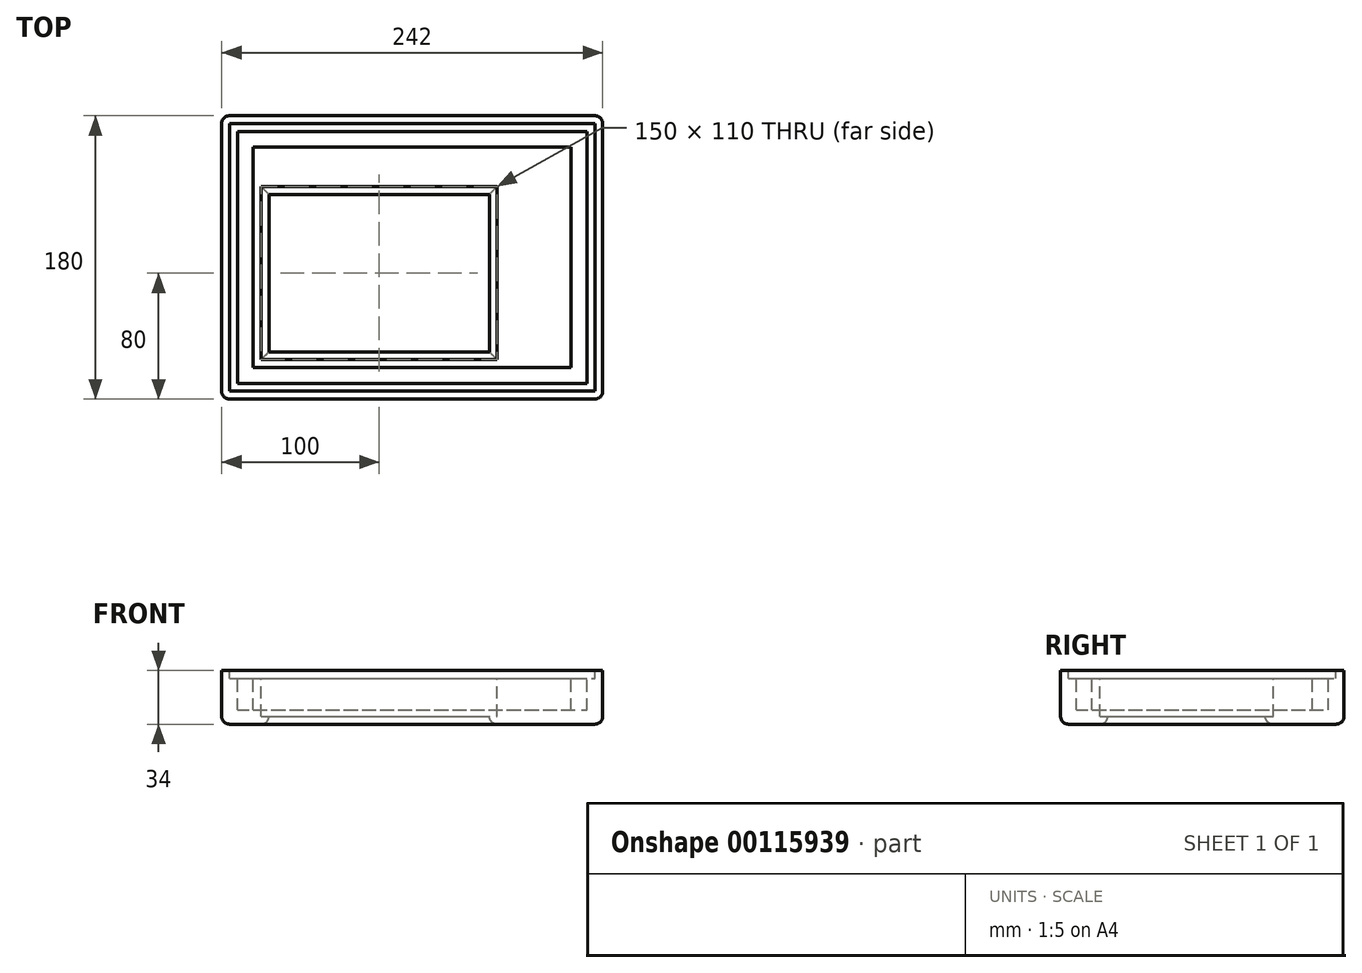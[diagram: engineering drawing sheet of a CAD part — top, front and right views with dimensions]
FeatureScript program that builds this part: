
annotation { "Feature Type Name" : "Feature", "Feature Type Description" : "" }
export const myFeature = defineFeature(function(context is Context, id is Id, definition is map)
    precondition{}
    {
        {
            var Q0;
            Q0=qCreatedBy(makeId("Top.planeOp"),FACE);
            var sketch = newSketch(context, id + "F0", { "sketchPlane" : qUnion([Q0])});
            skLineSegment(sketch, "E0.bottom", {"start": v(0, 0) * mm, "end": v(242, 0) * mm});
            skLineSegment(sketch, "E0.top", {"start": v(0, 180) * mm, "end": v(242, 180) * mm});
            skLineSegment(sketch, "E0.left", {"start": v(0, 0) * mm, "end": v(0, 180) * mm});
            skLineSegment(sketch, "E0.right", {"start": v(242, 0) * mm, "end": v(242, 180) * mm});
            skSolve(sketch);
        }
        {
            var Q0;
            Q0=makeQuery(id+"F0.imprint","IMPRINT",FACE,{"disambiguationData":[TD([[makeQuery(id+"F0.imprint","IMPRINT",EDGE,{"derivedFrom":sQuery(id+"F0.wireOp",EDGE,"E0.bottom")}),1.0]])]});
            extrude(context, id + "F1", {"entities" : qUnion([Q0]), "depth" : 34 * mm});
        }
        {
            var Q0;
            Q0=makeQuery(id+"F1.opExtrude","CAP_FACE",FACE,{"disambiguationData":[OSD([sQuery(id+"F0.wireOp",EDGE,"E0.bottom"),sQuery(id+"F0.wireOp",EDGE,"E0.top"),sQuery(id+"F0.wireOp",EDGE,"E0.left"),sQuery(id+"F0.wireOp",EDGE,"E0.right")])],"isStart":false});
            var sketch = newSketch(context, id + "F2", { "sketchPlane" : qUnion([Q0])});
            skPoint(sketch, "E1", {"position": v(30, 30) * mm});
            skLineSegment(sketch, "E2.bottom", {"start": v(30, 30) * mm, "end": v(170, 30) * mm});
            skLineSegment(sketch, "E2.top", {"start": v(30, 130) * mm, "end": v(170, 130) * mm});
            skLineSegment(sketch, "E2.left", {"start": v(30, 30) * mm, "end": v(30, 130) * mm});
            skLineSegment(sketch, "E2.right", {"start": v(170, 30) * mm, "end": v(170, 130) * mm});
            skSolve(sketch);
        }
        {
            var Q0;
            Q0=makeQuery(id+"F2.imprint","IMPRINT",FACE,{"disambiguationData":[TD([[makeQuery(id+"F2.imprint","IMPRINT",EDGE,{"derivedFrom":sQuery(id+"F2.wireOp",EDGE,"E2.bottom")}),1.0]])]});
            extrude(context, id + "F3", {"entities" : qUnion([Q0]), "operationType" : NewBodyOperationType.REMOVE, "endBound" : BoundingType.THROUGH_ALL, "oppositeDirection" : true, "depth" : 29 * mm});
        }
        {
            var Q0;
            Q0=makeQuery(id+"F1.opExtrude","CAP_FACE",FACE,{"disambiguationData":[OSD([sQuery(id+"F0.wireOp",EDGE,"E0.bottom"),sQuery(id+"F0.wireOp",EDGE,"E0.top"),sQuery(id+"F0.wireOp",EDGE,"E0.left"),sQuery(id+"F0.wireOp",EDGE,"E0.right")])],"isStart":false});
            var sketch = newSketch(context, id + "F4", { "sketchPlane" : qUnion([Q0])});
            skPoint(sketch, "E3", {"position": v(25, 25) * mm});
            skLineSegment(sketch, "E4.bottom", {"start": v(25, 25) * mm, "end": v(175, 25) * mm});
            skLineSegment(sketch, "E4.top", {"start": v(25, 135) * mm, "end": v(175, 135) * mm});
            skLineSegment(sketch, "E4.left", {"start": v(25, 25) * mm, "end": v(25, 135) * mm});
            skLineSegment(sketch, "E4.right", {"start": v(175, 25) * mm, "end": v(175, 135) * mm});
            skSolve(sketch);
        }
        {
            var Q0;
            Q0=makeQuery(id+"F4.imprint","IMPRINT",FACE,{"disambiguationData":[TD([[makeQuery(id+"F4.imprint","IMPRINT",EDGE,{"derivedFrom":sQuery(id+"F4.wireOp",EDGE,"E4.bottom")}),1.0]])]});
            extrude(context, id + "F5", {"entities" : qUnion([Q0]), "operationType" : NewBodyOperationType.REMOVE, "oppositeDirection" : true, "depth" : 29 * mm});
        }
        {
            var Q0;
            Q0=makeQuery(id+"F1.opExtrude","CAP_FACE",FACE,{"disambiguationData":[OSD([sQuery(id+"F0.wireOp",EDGE,"E0.bottom"),sQuery(id+"F0.wireOp",EDGE,"E0.top"),sQuery(id+"F0.wireOp",EDGE,"E0.left"),sQuery(id+"F0.wireOp",EDGE,"E0.right")])],"isStart":false});
            var sketch = newSketch(context, id + "F6", { "sketchPlane" : qUnion([Q0])});
            skPoint(sketch, "E5", {"position": v(5, 5) * mm});
            skLineSegment(sketch, "E6.bottom", {"start": v(5, 5) * mm, "end": v(237, 5) * mm});
            skLineSegment(sketch, "E6.top", {"start": v(5, 175) * mm, "end": v(237, 175) * mm});
            skLineSegment(sketch, "E6.left", {"start": v(5, 5) * mm, "end": v(5, 175) * mm});
            skLineSegment(sketch, "E6.right", {"start": v(237, 5) * mm, "end": v(237, 175) * mm});
            skSolve(sketch);
        }
        {
            var Q0;
            Q0=makeQuery(id+"F6.imprint","IMPRINT",FACE,{"disambiguationData":[TD([[makeQuery(id+"F6.imprint","IMPRINT",EDGE,{"derivedFrom":sQuery(id+"F6.wireOp",EDGE,"E6.bottom")}),1.0]])]});
            extrude(context, id + "F7", {"entities" : qUnion([Q0]), "operationType" : NewBodyOperationType.REMOVE, "oppositeDirection" : true, "depth" : 5 * mm});
        }
        {
            var Q0;
            Q0=makeQuery(id+"F7.boolean.opBoolean","COPY",FACE,{"derivedFrom":makeQuery(id+"F7.opExtrude","CAP_FACE",FACE,{"disambiguationData":[OSD([sQuery(id+"F4.wireOp",EDGE,"E4.bottom"),sQuery(id+"F4.wireOp",EDGE,"E4.top"),sQuery(id+"F4.wireOp",EDGE,"E4.left"),sQuery(id+"F4.wireOp",EDGE,"E4.right"),sQuery(id+"F6.wireOp",EDGE,"E6.bottom"),sQuery(id+"F6.wireOp",EDGE,"E6.top"),sQuery(id+"F6.wireOp",EDGE,"E6.left"),sQuery(id+"F6.wireOp",EDGE,"E6.right")])],"isStart":false})});
            var sketch = newSketch(context, id + "F8", { "sketchPlane" : qUnion([Q0])});
            skPoint(sketch, "E7", {"position": v(10, 10) * mm});
            skPoint(sketch, "E8", {"position": v(20, 20) * mm});
            skLineSegment(sketch, "E9.bottom", {"start": v(20, 20) * mm, "end": v(222, 20) * mm});
            skLineSegment(sketch, "E9.top", {"start": v(20, 160) * mm, "end": v(222, 160) * mm});
            skLineSegment(sketch, "E9.left", {"start": v(20, 20) * mm, "end": v(20, 160) * mm});
            skLineSegment(sketch, "E9.right", {"start": v(222, 20) * mm, "end": v(222, 160) * mm});
            skLineSegment(sketch, "E10.bottom", {"start": v(10, 10) * mm, "end": v(232, 10) * mm});
            skLineSegment(sketch, "E10.top", {"start": v(10, 170) * mm, "end": v(232, 170) * mm});
            skLineSegment(sketch, "E10.left", {"start": v(10, 10) * mm, "end": v(10, 170) * mm});
            skLineSegment(sketch, "E10.right", {"start": v(232, 10) * mm, "end": v(232, 170) * mm});
            skSolve(sketch);
        }
        {
            var Q0;
            Q0=makeQuery(id+"F8.imprint","IMPRINT",FACE,{"disambiguationData":[TD([[makeQuery(id+"F8.imprint","IMPRINT",EDGE,{"derivedFrom":sQuery(id+"F8.wireOp",EDGE,"E9.bottom")}),-1.0]])]});
            extrude(context, id + "F9", {"entities" : qUnion([Q0]), "operationType" : NewBodyOperationType.REMOVE, "oppositeDirection" : true, "depth" : 20 * mm});
        }
        {
            var Q0;
            Q0=makeQuery(id+"F1.opExtrude","SWEPT_EDGE",EDGE,{"disambiguationData":[OSD([sQuery(id+"F0.wireOp",EDGE,"E0.bottom"),sQuery(id+"F0.wireOp",EDGE,"E0.right")])]});
            var Q1;
            Q1=makeQuery(id+"F1.opExtrude","SWEPT_EDGE",EDGE,{"disambiguationData":[OSD([sQuery(id+"F0.wireOp",EDGE,"E0.top"),sQuery(id+"F0.wireOp",EDGE,"E0.right")])]});
            var Q2;
            Q2=makeQuery(id+"F1.opExtrude","SWEPT_EDGE",EDGE,{"disambiguationData":[OSD([sQuery(id+"F0.wireOp",EDGE,"E0.top"),sQuery(id+"F0.wireOp",EDGE,"E0.left")])]});
            var Q3;
            Q3=makeQuery(id+"F1.opExtrude","SWEPT_EDGE",EDGE,{"disambiguationData":[OSD([sQuery(id+"F0.wireOp",EDGE,"E0.bottom"),sQuery(id+"F0.wireOp",EDGE,"E0.left")])]});
            fillet(context, id + "F10", {"entities" : qUnion([Q0, Q1, Q2, Q3]), "radius" : 5 * mm, "tangentPropagation" : true, "allowEdgeOverflow" : false});
        }
        {
            var Q0;
            Q0=makeQuery(id+"F1.opExtrude","CAP_EDGE",EDGE,{"disambiguationData":[OSD([sQuery(id+"F0.wireOp",EDGE,"E0.bottom")])],"isStart":true});
            var Q1;
            Q1=makeQuery(id+"F3.boolean.opBoolean","INTERSECT",EDGE,{"derivedFrom":[makeQuery(id+"F1.opExtrude","CAP_FACE",FACE,{"disambiguationData":[OSD([sQuery(id+"F0.wireOp",EDGE,"E0.bottom"),sQuery(id+"F0.wireOp",EDGE,"E0.top"),sQuery(id+"F0.wireOp",EDGE,"E0.left"),sQuery(id+"F0.wireOp",EDGE,"E0.right")])],"isStart":true}),makeQuery(id+"F3.opExtrude","SWEPT_FACE",FACE,{"disambiguationData":[OSD([sQuery(id+"F2.wireOp",EDGE,"E2.right")])]})]});
            var Q2;
            Q2=makeQuery(id+"F3.boolean.opBoolean","INTERSECT",EDGE,{"derivedFrom":[makeQuery(id+"F1.opExtrude","CAP_FACE",FACE,{"disambiguationData":[OSD([sQuery(id+"F0.wireOp",EDGE,"E0.bottom"),sQuery(id+"F0.wireOp",EDGE,"E0.top"),sQuery(id+"F0.wireOp",EDGE,"E0.left"),sQuery(id+"F0.wireOp",EDGE,"E0.right")])],"isStart":true}),makeQuery(id+"F3.opExtrude","SWEPT_FACE",FACE,{"disambiguationData":[OSD([sQuery(id+"F2.wireOp",EDGE,"E2.bottom")])]})]});
            var Q3;
            Q3=makeQuery(id+"F3.boolean.opBoolean","INTERSECT",EDGE,{"derivedFrom":[makeQuery(id+"F1.opExtrude","CAP_FACE",FACE,{"disambiguationData":[OSD([sQuery(id+"F0.wireOp",EDGE,"E0.bottom"),sQuery(id+"F0.wireOp",EDGE,"E0.top"),sQuery(id+"F0.wireOp",EDGE,"E0.left"),sQuery(id+"F0.wireOp",EDGE,"E0.right")])],"isStart":true}),makeQuery(id+"F3.opExtrude","SWEPT_FACE",FACE,{"disambiguationData":[OSD([sQuery(id+"F2.wireOp",EDGE,"E2.left")])]})]});
            var Q4;
            Q4=makeQuery(id+"F3.boolean.opBoolean","INTERSECT",EDGE,{"derivedFrom":[makeQuery(id+"F1.opExtrude","CAP_FACE",FACE,{"disambiguationData":[OSD([sQuery(id+"F0.wireOp",EDGE,"E0.bottom"),sQuery(id+"F0.wireOp",EDGE,"E0.top"),sQuery(id+"F0.wireOp",EDGE,"E0.left"),sQuery(id+"F0.wireOp",EDGE,"E0.right")])],"isStart":true}),makeQuery(id+"F3.opExtrude","SWEPT_FACE",FACE,{"disambiguationData":[OSD([sQuery(id+"F2.wireOp",EDGE,"E2.top")])]})]});
            fillet(context, id + "F11", {"entities" : qUnion([Q0, Q1, Q2, Q3, Q4]), "radius" : 5 * mm, "tangentPropagation" : true, "allowEdgeOverflow" : false});
        }
    });
